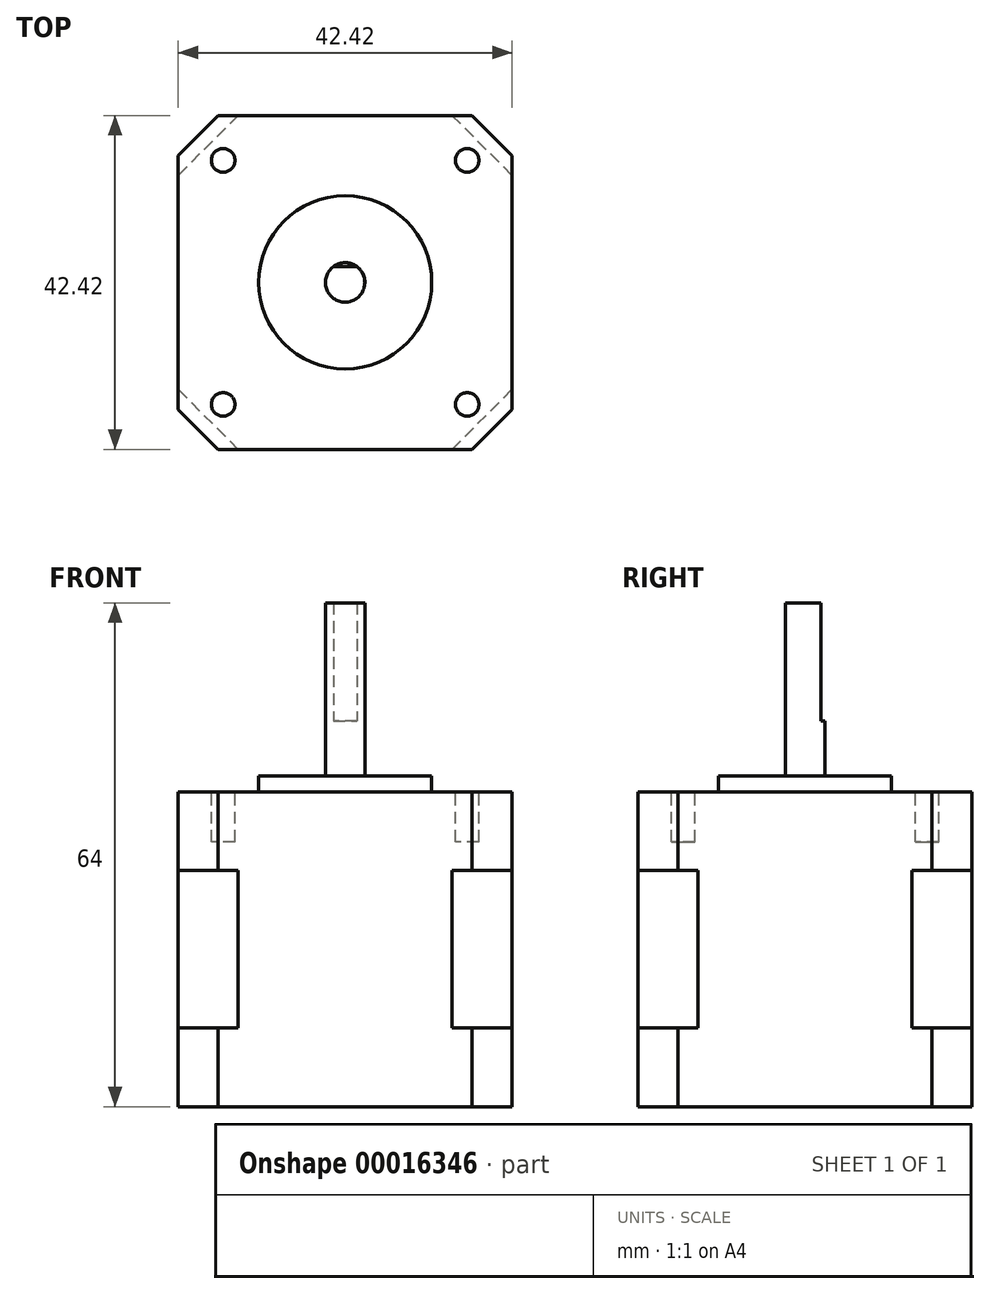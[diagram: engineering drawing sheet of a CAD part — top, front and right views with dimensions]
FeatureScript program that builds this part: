
annotation { "Feature Type Name" : "Feature", "Feature Type Description" : "" }
export const myFeature = defineFeature(function(context is Context, id is Id, definition is map)
    precondition{}
    {
        {
            var Q0;
            Q0=qCreatedBy(makeId("Top.planeOp"),FACE);
            var sketch = newSketch(context, id + "F0", { "sketchPlane" : qUnion([Q0])});
            skLineSegment(sketch, "E0.bottom", {"start": v(-21.2, 21.2) * mm, "end": v(21.2, 21.2) * mm});
            skLineSegment(sketch, "E0.top", {"start": v(-21.2, -21.2) * mm, "end": v(21.2, -21.2) * mm});
            skLineSegment(sketch, "E0.left", {"start": v(-21.2, 21.2) * mm, "end": v(-21.2, -21.2) * mm});
            skLineSegment(sketch, "E0.right", {"start": v(21.2, 21.2) * mm, "end": v(21.2, -21.2) * mm});
            skSolve(sketch);
        }
        {
            var Q0;
            Q0=makeQuery(id+"F0.imprint","IMPRINT",FACE,{"disambiguationData":[TD([[makeQuery(id+"F0.imprint","IMPRINT",EDGE,{"derivedFrom":sQuery(id+"F0.wireOp",EDGE,"E0.bottom")}),-1.0]])]});
            extrude(context, id + "F1", {"entities" : qUnion([Q0]), "endBound" : BoundingType.SYMMETRIC, "depth" : 20 * mm});
        }
        {
            var Q0;
            Q0=makeQuery(id+"F1.opExtrude","SWEPT_EDGE",EDGE,{"disambiguationData":[OSD([sQuery(id+"F0.wireOp",EDGE,"E0.bottom"),sQuery(id+"F0.wireOp",EDGE,"E0.right")])]});
            var Q1;
            Q1=makeQuery(id+"F1.opExtrude","SWEPT_EDGE",EDGE,{"disambiguationData":[OSD([sQuery(id+"F0.wireOp",EDGE,"E0.bottom"),sQuery(id+"F0.wireOp",EDGE,"E0.left")])]});
            var Q2;
            Q2=makeQuery(id+"F1.opExtrude","SWEPT_EDGE",EDGE,{"disambiguationData":[OSD([sQuery(id+"F0.wireOp",EDGE,"E0.top"),sQuery(id+"F0.wireOp",EDGE,"E0.left")])]});
            var Q3;
            Q3=makeQuery(id+"F1.opExtrude","SWEPT_EDGE",EDGE,{"disambiguationData":[OSD([sQuery(id+"F0.wireOp",EDGE,"E0.top"),sQuery(id+"F0.wireOp",EDGE,"E0.right")])]});
            chamfer(context, id + "F2", {"entities" : qUnion([Q0, Q1, Q2, Q3]), "width" : 7.62 * mm, "tangentPropagation" : true});
        }
        {
            var Q0;
            Q0=makeQuery(id+"F1.opExtrude","CAP_FACE",FACE,{"disambiguationData":[OSD([sQuery(id+"F0.wireOp",EDGE,"E0.bottom"),sQuery(id+"F0.wireOp",EDGE,"E0.top"),sQuery(id+"F0.wireOp",EDGE,"E0.left"),sQuery(id+"F0.wireOp",EDGE,"E0.right")])],"isStart":false});
            var sketch = newSketch(context, id + "F3", { "sketchPlane" : qUnion([Q0])});
            skLineSegment(sketch, "E1.bottom", {"start": v(-21.2, 21.2) * mm, "end": v(21.2, 21.2) * mm});
            skLineSegment(sketch, "E1.top", {"start": v(-21.2, -21.2) * mm, "end": v(21.2, -21.2) * mm});
            skLineSegment(sketch, "E1.left", {"start": v(-21.2, 21.2) * mm, "end": v(-21.2, -21.2) * mm});
            skLineSegment(sketch, "E1.right", {"start": v(21.2, 21.2) * mm, "end": v(21.2, -21.2) * mm});
            skSolve(sketch);
        }
        {
            var Q0;
            {var subQ0=sQuery(id+"F0.wireOp",EDGE,"E0.top");var subQ1=sQuery(id+"F0.wireOp",EDGE,"E0.right");var subQ2=sQuery(id+"F0.wireOp",EDGE,"E0.bottom");var subQ3=sQuery(id+"F0.wireOp",EDGE,"E0.left");var subQ4=makeQuery(id+"F1.opExtrude","CAP_FACE",FACE,{"disambiguationData":[OSD([subQ2,subQ0,subQ3,subQ1])],"isStart":false});var subQ8=makeQuery(id+"F2.opChamfer","BLEND_EDGE",EDGE,{"blendedFrom":[makeQuery(id+"F1.opExtrude","SWEPT_EDGE",EDGE,{"disambiguationData":[OSD([subQ2,subQ3])]}),subQ4],"blendedInto":[subQ4]});Q0=makeQuery(id+"F3.imprint","IMPRINT",FACE,{"disambiguationData":[TD([[makeQuery(id+"F3.imprint","IMPRINT",EDGE,{"derivedFrom":subQ8}),1.0]])]});}
            var Q1;
            {var subQ0=sQuery(id+"F0.wireOp",EDGE,"E0.bottom");var subQ1=sQuery(id+"F0.wireOp",EDGE,"E0.right");var subQ2=makeQuery(id+"F2.opChamfer","BLEND_EDGE",EDGE,{"blendedFrom":[makeQuery(id+"F1.opExtrude","SWEPT_EDGE",EDGE,{"disambiguationData":[OSD([subQ0,subQ1])]}),makeQuery(id+"F1.opExtrude","CAP_FACE",FACE,{"disambiguationData":[OSD([subQ0,sQuery(id+"F0.wireOp",EDGE,"E0.top"),sQuery(id+"F0.wireOp",EDGE,"E0.left"),subQ1])],"isStart":false})],"blendedInto":[makeQuery(id+"F1.opExtrude","CAP_FACE",FACE,{"disambiguationData":[OSD([subQ0,sQuery(id+"F0.wireOp",EDGE,"E0.top"),sQuery(id+"F0.wireOp",EDGE,"E0.left"),subQ1])],"isStart":false})]});Q1=makeQuery(id+"F3.imprint","IMPRINT",FACE,{"disambiguationData":[TD([[makeQuery(id+"F3.imprint","IMPRINT",EDGE,{"derivedFrom":subQ2}),-1.0]])]});}
            var Q2;
            {var subQ0=sQuery(id+"F0.wireOp",EDGE,"E0.bottom");var subQ1=sQuery(id+"F0.wireOp",EDGE,"E0.left");var subQ2=makeQuery(id+"F2.opChamfer","BLEND_EDGE",EDGE,{"blendedFrom":[makeQuery(id+"F1.opExtrude","SWEPT_EDGE",EDGE,{"disambiguationData":[OSD([subQ0,subQ1])]}),makeQuery(id+"F1.opExtrude","CAP_FACE",FACE,{"disambiguationData":[OSD([subQ0,sQuery(id+"F0.wireOp",EDGE,"E0.top"),subQ1,sQuery(id+"F0.wireOp",EDGE,"E0.right")])],"isStart":false})],"blendedInto":[makeQuery(id+"F1.opExtrude","CAP_FACE",FACE,{"disambiguationData":[OSD([subQ0,sQuery(id+"F0.wireOp",EDGE,"E0.top"),subQ1,sQuery(id+"F0.wireOp",EDGE,"E0.right")])],"isStart":false})]});Q2=makeQuery(id+"F3.imprint","IMPRINT",FACE,{"disambiguationData":[TD([[makeQuery(id+"F3.imprint","IMPRINT",EDGE,{"derivedFrom":subQ2}),-1.0]])]});}
            var Q3;
            {var subQ0=sQuery(id+"F0.wireOp",EDGE,"E0.top");var subQ1=sQuery(id+"F0.wireOp",EDGE,"E0.left");var subQ2=makeQuery(id+"F2.opChamfer","BLEND_EDGE",EDGE,{"blendedFrom":[makeQuery(id+"F1.opExtrude","SWEPT_EDGE",EDGE,{"disambiguationData":[OSD([subQ0,subQ1])]}),makeQuery(id+"F1.opExtrude","CAP_FACE",FACE,{"disambiguationData":[OSD([sQuery(id+"F0.wireOp",EDGE,"E0.bottom"),subQ0,subQ1,sQuery(id+"F0.wireOp",EDGE,"E0.right")])],"isStart":false})],"blendedInto":[makeQuery(id+"F1.opExtrude","CAP_FACE",FACE,{"disambiguationData":[OSD([sQuery(id+"F0.wireOp",EDGE,"E0.bottom"),subQ0,subQ1,sQuery(id+"F0.wireOp",EDGE,"E0.right")])],"isStart":false})]});Q3=makeQuery(id+"F3.imprint","IMPRINT",FACE,{"disambiguationData":[TD([[makeQuery(id+"F3.imprint","IMPRINT",EDGE,{"derivedFrom":subQ2}),-1.0]])]});}
            var Q4;
            {var subQ0=sQuery(id+"F0.wireOp",EDGE,"E0.top");var subQ1=sQuery(id+"F0.wireOp",EDGE,"E0.right");var subQ2=makeQuery(id+"F2.opChamfer","BLEND_EDGE",EDGE,{"blendedFrom":[makeQuery(id+"F1.opExtrude","SWEPT_EDGE",EDGE,{"disambiguationData":[OSD([subQ0,subQ1])]}),makeQuery(id+"F1.opExtrude","CAP_FACE",FACE,{"disambiguationData":[OSD([sQuery(id+"F0.wireOp",EDGE,"E0.bottom"),subQ0,sQuery(id+"F0.wireOp",EDGE,"E0.left"),subQ1])],"isStart":false})],"blendedInto":[makeQuery(id+"F1.opExtrude","CAP_FACE",FACE,{"disambiguationData":[OSD([sQuery(id+"F0.wireOp",EDGE,"E0.bottom"),subQ0,sQuery(id+"F0.wireOp",EDGE,"E0.left"),subQ1])],"isStart":false})]});Q4=makeQuery(id+"F3.imprint","IMPRINT",FACE,{"disambiguationData":[TD([[makeQuery(id+"F3.imprint","IMPRINT",EDGE,{"derivedFrom":subQ2}),-1.0]])]});}
            extrude(context, id + "F4", {"entities" : qUnion([Q0, Q1, Q2, Q3, Q4]), "operationType" : NewBodyOperationType.ADD, "depth" : 10 * mm});
        }
        {
            var Q0;
            Q0=makeQuery(id+"F4.opExtrude","SWEPT_EDGE",EDGE,{"disambiguationData":[OSD([sQuery(id+"F3.wireOp",EDGE,"E1.bottom"),sQuery(id+"F3.wireOp",EDGE,"E1.right")])]});
            var Q1;
            Q1=makeQuery(id+"F4.opExtrude","SWEPT_EDGE",EDGE,{"disambiguationData":[OSD([sQuery(id+"F3.wireOp",EDGE,"E1.bottom"),sQuery(id+"F3.wireOp",EDGE,"E1.left")])]});
            var Q2;
            Q2=makeQuery(id+"F4.opExtrude","SWEPT_EDGE",EDGE,{"disambiguationData":[OSD([sQuery(id+"F3.wireOp",EDGE,"E1.top"),sQuery(id+"F3.wireOp",EDGE,"E1.left")])]});
            var Q3;
            Q3=makeQuery(id+"F4.opExtrude","SWEPT_EDGE",EDGE,{"disambiguationData":[OSD([sQuery(id+"F3.wireOp",EDGE,"E1.top"),sQuery(id+"F3.wireOp",EDGE,"E1.right")])]});
            chamfer(context, id + "F5", {"entities" : qUnion([Q0, Q1, Q2, Q3]), "width" : 5.08 * mm, "tangentPropagation" : true});
        }
        {
            var Q0;
            Q0=makeQuery(id+"F1.opExtrude","CAP_FACE",FACE,{"disambiguationData":[OSD([sQuery(id+"F0.wireOp",EDGE,"E0.bottom"),sQuery(id+"F0.wireOp",EDGE,"E0.top"),sQuery(id+"F0.wireOp",EDGE,"E0.left"),sQuery(id+"F0.wireOp",EDGE,"E0.right")])],"isStart":true});
            var sketch = newSketch(context, id + "F6", { "sketchPlane" : qUnion([Q0])});
            skLineSegment(sketch, "E2.0.0", {"start": v(-16.13, 21.2) * mm, "end": v(16.13, 21.2) * mm});
            skLineSegment(sketch, "E2.0.1", {"start": v(16.13, 21.2) * mm, "end": v(21.2, 16.13) * mm});
            skLineSegment(sketch, "E2.0.2", {"start": v(21.2, -16.13) * mm, "end": v(21.2, 16.13) * mm});
            skLineSegment(sketch, "E2.0.3", {"start": v(21.2, -16.13) * mm, "end": v(16.13, -21.2) * mm});
            skLineSegment(sketch, "E2.0.4", {"start": v(-16.13, -21.2) * mm, "end": v(16.13, -21.2) * mm});
            skLineSegment(sketch, "E2.0.5", {"start": v(-16.13, -21.2) * mm, "end": v(-21.2, -16.13) * mm});
            skLineSegment(sketch, "E2.0.6", {"start": v(-21.2, -16.13) * mm, "end": v(-21.2, 16.13) * mm});
            skLineSegment(sketch, "E2.0.7", {"start": v(-21.2, 16.13) * mm, "end": v(-16.13, 21.2) * mm});
            skSolve(sketch);
        }
        {
            var Q0;
            {var subQ3=sQuery(id+"F6.wireOp",EDGE,"E2.0.7");Q0=makeQuery(id+"F6.imprint","IMPRINT",FACE,{"disambiguationData":[TD([[makeQuery(id+"F6.imprint","IMPRINT",EDGE,{"derivedFrom":subQ3}),-1.0]])]});}
            var Q1;
            {var subQ4=sQuery(id+"F6.wireOp",EDGE,"E2.0.1");Q1=makeQuery(id+"F6.imprint","IMPRINT",FACE,{"disambiguationData":[TD([[makeQuery(id+"F6.imprint","IMPRINT",EDGE,{"derivedFrom":subQ4}),-1.0]])]});}
            var Q2;
            {var subQ4=sQuery(id+"F6.wireOp",EDGE,"E2.0.3");Q2=makeQuery(id+"F6.imprint","IMPRINT",FACE,{"disambiguationData":[TD([[makeQuery(id+"F6.imprint","IMPRINT",EDGE,{"derivedFrom":subQ4}),-1.0]])]});}
            var Q3;
            {var subQ4=sQuery(id+"F6.wireOp",EDGE,"E2.0.5");Q3=makeQuery(id+"F6.imprint","IMPRINT",FACE,{"disambiguationData":[TD([[makeQuery(id+"F6.imprint","IMPRINT",EDGE,{"derivedFrom":subQ4}),-1.0]])]});}
            var Q4;
            {var subQ0=sQuery(id+"F0.wireOp",EDGE,"E0.top");var subQ1=sQuery(id+"F0.wireOp",EDGE,"E0.right");var subQ2=sQuery(id+"F0.wireOp",EDGE,"E0.bottom");var subQ3=sQuery(id+"F0.wireOp",EDGE,"E0.left");var subQ4=makeQuery(id+"F1.opExtrude","CAP_FACE",FACE,{"disambiguationData":[OSD([subQ2,subQ0,subQ3,subQ1])],"isStart":true});var subQ8=makeQuery(id+"F2.opChamfer","BLEND_EDGE",EDGE,{"blendedFrom":[makeQuery(id+"F1.opExtrude","SWEPT_EDGE",EDGE,{"disambiguationData":[OSD([subQ2,subQ3])]}),subQ4],"blendedInto":[subQ4]});Q4=makeQuery(id+"F6.imprint","IMPRINT",FACE,{"disambiguationData":[TD([[makeQuery(id+"F6.imprint","IMPRINT",EDGE,{"derivedFrom":subQ8}),1.0]])]});}
            extrude(context, id + "F7", {"entities" : qUnion([Q0, Q1, Q2, Q3, Q4]), "operationType" : NewBodyOperationType.ADD, "depth" : 10 * mm});
        }
        {
            var Q0;
            Q0=makeQuery(id+"F4.opExtrude","CAP_FACE",FACE,{"disambiguationData":[OSD([sQuery(id+"F3.wireOp",EDGE,"E1.bottom"),sQuery(id+"F3.wireOp",EDGE,"E1.top"),sQuery(id+"F3.wireOp",EDGE,"E1.left"),sQuery(id+"F3.wireOp",EDGE,"E1.right")])],"isStart":false});
            var sketch = newSketch(context, id + "F8", { "sketchPlane" : qUnion([Q0])});
            skCircle(sketch, "E3", {"center": v(0, 0) * mm, "radius": 11 * mm});
            skSolve(sketch);
        }
        {
            var Q0;
            Q0=makeQuery(id+"F8.imprint","IMPRINT",FACE,{"disambiguationData":[TD([[makeQuery(id+"F8.imprint","IMPRINT",EDGE,{"derivedFrom":sQuery(id+"F8.wireOp",EDGE,"E3")}),1.0]])]});
            extrude(context, id + "F9", {"entities" : qUnion([Q0]), "operationType" : NewBodyOperationType.ADD, "depth" : 2 * mm});
        }
        {
            var Q0;
            Q0=makeQuery(id+"F9.opExtrude","CAP_FACE",FACE,{"disambiguationData":[OSD([sQuery(id+"F8.wireOp",EDGE,"E3")])],"isStart":false});
            var sketch = newSketch(context, id + "F10", { "sketchPlane" : qUnion([Q0])});
            skCircle(sketch, "E4", {"center": v(0, 0) * mm, "radius": 2.5 * mm});
            skSolve(sketch);
        }
        {
            var Q0;
            Q0=makeQuery(id+"F10.imprint","IMPRINT",FACE,{"disambiguationData":[TD([[makeQuery(id+"F10.imprint","IMPRINT",EDGE,{"derivedFrom":sQuery(id+"F10.wireOp",EDGE,"E4")}),1.0]])]});
            extrude(context, id + "F11", {"entities" : qUnion([Q0]), "operationType" : NewBodyOperationType.ADD, "depth" : 22 * mm});
        }
        {
            var Q0;
            Q0=makeQuery(id+"F11.opExtrude","CAP_FACE",FACE,{"disambiguationData":[OSD([sQuery(id+"F10.wireOp",EDGE,"E4")])],"isStart":false});
            var sketch = newSketch(context, id + "F12", { "sketchPlane" : qUnion([Q0])});
            skLineSegment(sketch, "E5.bottom", {"start": v(-2.63, 2.93) * mm, "end": v(2.62, 2.93) * mm});
            skLineSegment(sketch, "E5.top", {"start": v(-2.63, 2) * mm, "end": v(2.62, 2) * mm});
            skLineSegment(sketch, "E5.left", {"start": v(-2.63, 2.93) * mm, "end": v(-2.63, 2) * mm});
            skLineSegment(sketch, "E5.right", {"start": v(2.62, 2.93) * mm, "end": v(2.62, 2) * mm});
            skSolve(sketch);
        }
        {
            var Q0;
            {var subQ0=makeQuery(id+"F11.opExtrude","CAP_EDGE",EDGE,{"disambiguationData":[OSD([sQuery(id+"F10.wireOp",EDGE,"E4")])],"isStart":false});var subQ1=sQuery(id+"F12.wireOp",EDGE,"E5.top");var subQ3=makeQuery(id+"F12.imprint","INTERSECT",VERTEX,{"disambiguationData":[OD(0.0)],"derivedFrom":[subQ0,subQ1]});Q0=qUnion([makeQuery(id+"F12.imprint","IMPRINT",FACE,{"disambiguationData":[TD([[makeQuery(id+"F12.imprint","IMPRINT",EDGE,{"derivedFrom":sQuery(id+"F12.wireOp",EDGE,"E5.bottom")}),-1.0]])]}),makeQuery(id+"F12.imprint","IMPRINT",FACE,{"disambiguationData":[TD([[makeQuery(id+"F12.imprint","IMPRINT",EDGE,{"disambiguationData":[TD([[subQ3,-1.0]])],"derivedFrom":subQ1}),1.0]])]})]);}
            extrude(context, id + "F13", {"entities" : qUnion([Q0]), "operationType" : NewBodyOperationType.REMOVE, "oppositeDirection" : true, "depth" : 15 * mm});
        }
        {
            var Q0;
            Q0=makeQuery(id+"F4.opExtrude","CAP_FACE",FACE,{"disambiguationData":[OSD([sQuery(id+"F3.wireOp",EDGE,"E1.bottom"),sQuery(id+"F3.wireOp",EDGE,"E1.top"),sQuery(id+"F3.wireOp",EDGE,"E1.left"),sQuery(id+"F3.wireOp",EDGE,"E1.right")])],"isStart":false});
            var sketch = newSketch(context, id + "F14", { "sketchPlane" : qUnion([Q0])});
            skCircle(sketch, "E6", {"center": v(-15.5, 15.5) * mm, "radius": 1.5 * mm});
            skCircle(sketch, "E7", {"center": v(15.5, 15.5) * mm, "radius": 1.5 * mm});
            skCircle(sketch, "E8", {"center": v(15.5, -15.5) * mm, "radius": 1.5 * mm});
            skCircle(sketch, "E9", {"center": v(-15.5, -15.5) * mm, "radius": 1.5 * mm});
            skLineSegment(sketch, "E10", {"start": v(-45.53, 0) * mm, "end": v(50.04, 0) * mm, "construction": true});
            skLineSegment(sketch, "E11", {"start": v(0, -35.63) * mm, "end": v(0, 35.98) * mm, "construction": true});
            skLineSegment(sketch, "E12.rect.bottom", {"start": v(-15.5, 15.5) * mm, "end": v(15.5, 15.5) * mm, "construction": true});
            skLineSegment(sketch, "E12.rect.top", {"start": v(-15.5, -15.5) * mm, "end": v(15.5, -15.5) * mm, "construction": true});
            skLineSegment(sketch, "E12.rect.left", {"start": v(-15.5, 15.5) * mm, "end": v(-15.5, -15.5) * mm, "construction": true});
            skLineSegment(sketch, "E12.rect.right", {"start": v(15.5, 15.5) * mm, "end": v(15.5, -15.5) * mm, "construction": true});
            skPoint(sketch, "E12.rect.middle", {"position": v(0, 0) * mm});
            skPoint(sketch, "E13", {"position": v(0, 15.5) * mm});
            skSolve(sketch);
        }
        {
            var Q0;
            {Q0=qUnion([makeQuery(id+"F14.imprint","IMPRINT",FACE,{"disambiguationData":[TD([[makeQuery(id+"F14.imprint","IMPRINT",EDGE,{"derivedFrom":sQuery(id+"F14.wireOp",EDGE,"E6")}),1.0]])]}),makeQuery(id+"F14.imprint","IMPRINT",FACE,{"disambiguationData":[TD([[makeQuery(id+"F14.imprint","IMPRINT",EDGE,{"derivedFrom":sQuery(id+"F14.wireOp",EDGE,"E7")}),1.0]])]}),makeQuery(id+"F14.imprint","IMPRINT",FACE,{"disambiguationData":[TD([[makeQuery(id+"F14.imprint","IMPRINT",EDGE,{"derivedFrom":sQuery(id+"F14.wireOp",EDGE,"E8")}),1.0]])]}),makeQuery(id+"F14.imprint","IMPRINT",FACE,{"disambiguationData":[TD([[makeQuery(id+"F14.imprint","IMPRINT",EDGE,{"derivedFrom":sQuery(id+"F14.wireOp",EDGE,"E9")}),1.0]])]})]);}
            extrude(context, id + "F15", {"entities" : qUnion([Q0]), "operationType" : NewBodyOperationType.REMOVE, "oppositeDirection" : true, "depth" : 6.35 * mm});
        }
    });
